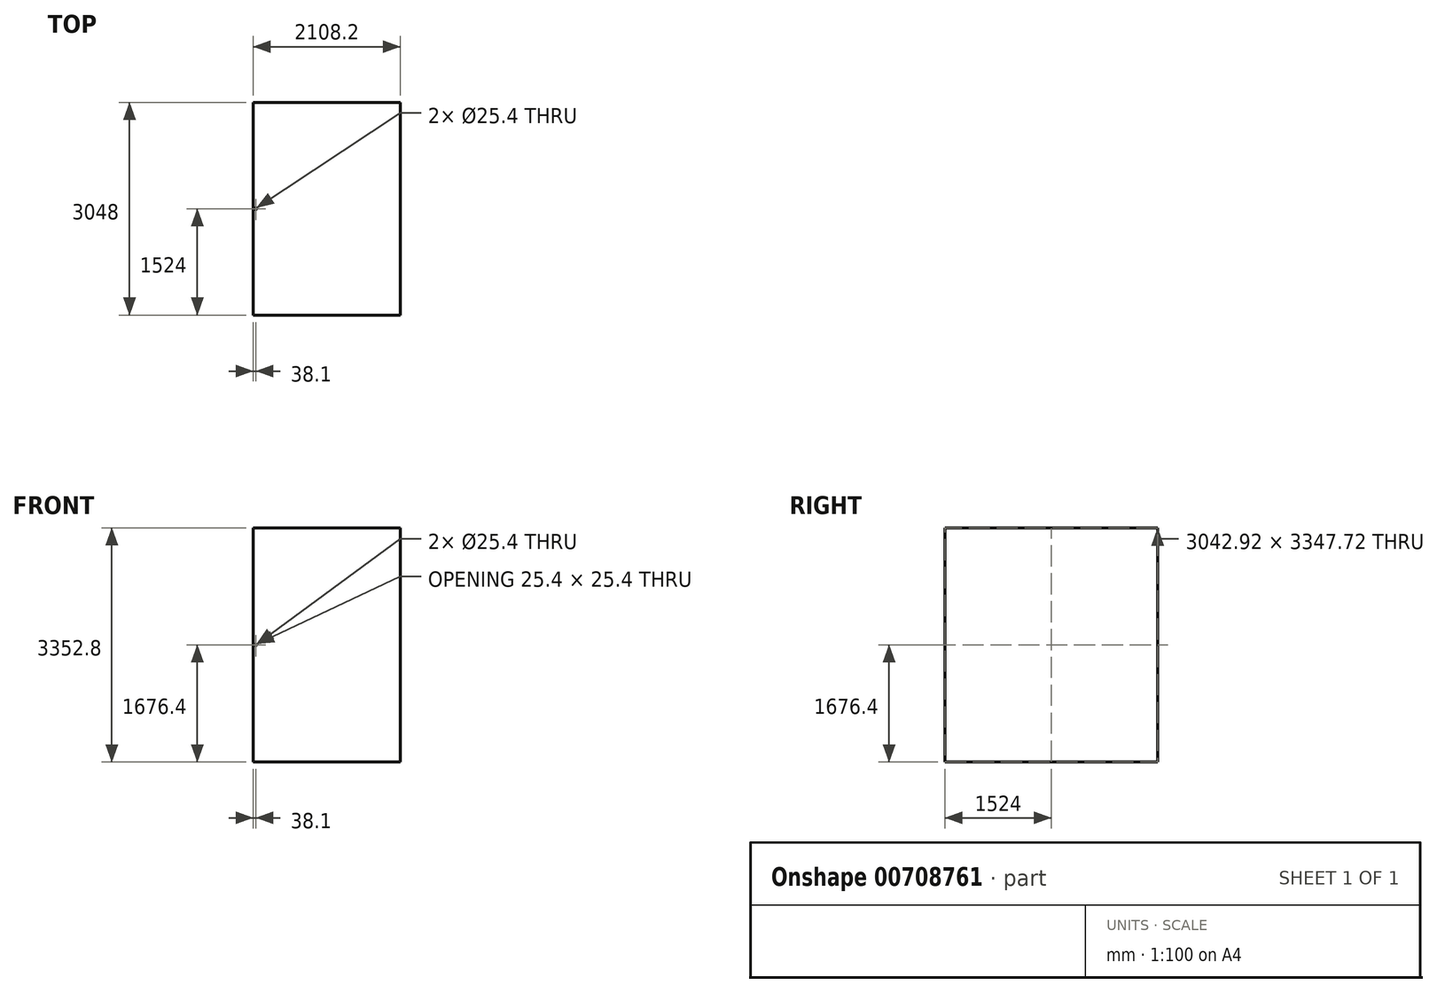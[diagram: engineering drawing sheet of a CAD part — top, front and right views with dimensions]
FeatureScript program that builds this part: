
annotation { "Feature Type Name" : "Feature", "Feature Type Description" : "" }
export const myFeature = defineFeature(function(context is Context, id is Id, definition is map)
    precondition{}
    {
        {
            var Q0;
            Q0=qCreatedBy(makeId("Front.planeOp"),FACE);
            var sketch = newSketch(context, id + "F0", { "sketchPlane" : qUnion([Q0])});
            skLineSegment(sketch, "E0", {"start": v(0, 0) * mm, "end": v(0, 3352.8) * mm});
            skLineSegment(sketch, "E1", {"start": v(0, 3352.8) * mm, "end": v(2108.2, 3352.8) * mm});
            skLineSegment(sketch, "E2", {"start": v(2108.2, 3352.8) * mm, "end": v(2108.2, 0) * mm});
            skLineSegment(sketch, "E3", {"start": v(2108.2, 0) * mm, "end": v(0, 0) * mm});
            skSolve(sketch);
        }
        {
            var Q0;
            Q0 = qSketchRegion(id + "F0", true);
            extrude(context, id + "F1", {"entities" : qUnion([Q0]), "depth" : 3048 * mm, "offsetDistance" : 25.4 * mm});
        }
        {
            var Q0;
            Q0=makeQuery(id+"F1.opExtrude","SWEPT_FACE",FACE,{"disambiguationData":[OSD([sQuery(id+"F0.wireOp",EDGE,"E2")])]});
            var sketch = newSketch(context, id + "F2", { "sketchPlane" : qUnion([Q0])});
            skLineSegment(sketch, "E4.bottom", {"start": v(-3045.46, 2.54) * mm, "end": v(-2.54, 2.54) * mm});
            skLineSegment(sketch, "E4.top", {"start": v(-3045.46, 3350.26) * mm, "end": v(-2.54, 3350.26) * mm});
            skLineSegment(sketch, "E4.left", {"start": v(-3045.46, 2.54) * mm, "end": v(-3045.46, 3350.26) * mm});
            skLineSegment(sketch, "E4.right", {"start": v(-2.54, 2.54) * mm, "end": v(-2.54, 3350.26) * mm});
            skSolve(sketch);
        }
        {
            var Q0;
            Q0=makeQuery(id+"F2.imprint","IMPRINT",FACE,{"disambiguationData":[TD([[makeQuery(id+"F2.imprint","IMPRINT",EDGE,{"derivedFrom":sQuery(id+"F2.wireOp",EDGE,"E4.bottom")}),1.0]])]});
            extrude(context, id + "F3", {"entities" : qUnion([Q0]), "operationType" : NewBodyOperationType.REMOVE, "endBound" : BoundingType.UP_TO_NEXT, "oppositeDirection" : true, "depth" : 25.4 * mm, "offsetDistance" : 25.4 * mm});
        }
        {
            var Q0;
            Q0=makeQuery(id+"F1.opExtrude","CAP_FACE",FACE,{"disambiguationData":[OSD([sQuery(id+"F0.wireOp",EDGE,"E0"),sQuery(id+"F0.wireOp",EDGE,"E1"),sQuery(id+"F0.wireOp",EDGE,"E2"),sQuery(id+"F0.wireOp",EDGE,"E3")])],"isStart":false});
            var sketch = newSketch(context, id + "F4", { "sketchPlane" : qUnion([Q0])});
            skPoint(sketch, "E5", {"position": v(38.1, 1676.4) * mm});
            skSolve(sketch);
        }
        {
            var Q0;
            Q0=sQuery(id+"F4.wireOp",VERTEX,"E5");
            var Q1;
            Q1=makeQuery(id+"F1.opExtrude","SWEPT_BODY",BODY,{"disambiguationData":[OSD([sQuery(id+"F0.wireOp",EDGE,"E0"),sQuery(id+"F0.wireOp",EDGE,"E1"),sQuery(id+"F0.wireOp",EDGE,"E2"),sQuery(id+"F0.wireOp",EDGE,"E3")])]});
            hole(context, id + "F5", {"style" : HoleStyle.SIMPLE, "endStyle" : HoleEndStyle.THROUGH, "holeDiameter" : 25.4 * mm, "majorDiameter" : 6.35 * mm, "isTappedThrough" : true, "tappedDepth" : 12.7 * mm, "tapClearance" : 3, "locations" : qUnion([Q0]), "scope" : qUnion([Q1])});
        }
        {
            var Q0;
            Q0=makeQuery(id+"F1.opExtrude","SWEPT_FACE",FACE,{"disambiguationData":[OSD([sQuery(id+"F0.wireOp",EDGE,"E1")])]});
            var sketch = newSketch(context, id + "F6", { "sketchPlane" : qUnion([Q0])});
            skPoint(sketch, "E6", {"position": v(38.1, -1524) * mm});
            skSolve(sketch);
        }
        {
            var Q0;
            Q0=sQuery(id+"F6.wireOp",VERTEX,"E6");
            var Q1;
            Q1=makeQuery(id+"F1.opExtrude","SWEPT_BODY",BODY,{"disambiguationData":[OSD([sQuery(id+"F0.wireOp",EDGE,"E0"),sQuery(id+"F0.wireOp",EDGE,"E1"),sQuery(id+"F0.wireOp",EDGE,"E2"),sQuery(id+"F0.wireOp",EDGE,"E3")])]});
            hole(context, id + "F7", {"style" : HoleStyle.SIMPLE, "endStyle" : HoleEndStyle.THROUGH, "holeDiameter" : 25.4 * mm, "majorDiameter" : 6.35 * mm, "isTappedThrough" : true, "tappedDepth" : 12.7 * mm, "tapClearance" : 3, "locations" : qUnion([Q0]), "scope" : qUnion([Q1])});
        }
    });
